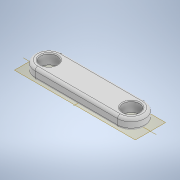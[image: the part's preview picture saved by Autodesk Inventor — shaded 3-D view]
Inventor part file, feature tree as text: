
AUTODESK INVENTOR PART (.ipt)
format: ipt  version: 2020 (Build 240168000, 168)  size: 151,552 bytes
history: native  units: mm
features: fillet x2, other x1, extrude x1, sketch x1
ambient origin geometry x8: Origin, YZ Plane, XZ Plane, XY Plane, X Axis, Y Axis, Z Axis, Center Point
bodies: Body1 (feature_tree)
feature tree (5):
  other  "Твердое тело1"
  extrude  "Выдавливание1"  Depth=30.0mm
  fillet  "Сопряжение1"  Radius=10.0mm
  fillet  "Сопряжение2"  Radius=6.0mm
  sketch  "Эскиз1"
